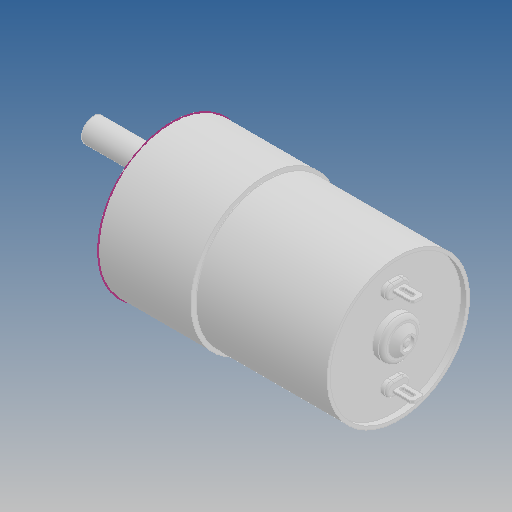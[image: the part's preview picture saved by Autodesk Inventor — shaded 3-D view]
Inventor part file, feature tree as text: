
AUTODESK INVENTOR PART (.ipt)
format: ipt  version: 2020 (Build 240168000, 168)  size: 274,432 bytes
history: native  units: mm
features: other x4, sketch x2
ambient origin geometry x8: Origin, YZ Plane, XZ Plane, XY Plane, X Axis, Y Axis, Z Axis, Center Point
bodies: Body1 (feature_tree)
feature tree (6):
  other  "dc_gear_motor_12V_500rpm.ipt"
  other  "Solid1::dc_gear_motor_12V_500rpm.ipt"
  other  "Элемент создания тегов1"
  sketch  "Sketch1"  dims[d0=10.0mm]
  sketch  "Sketch2"
  other  "Твердое тело1"
